# Revit family: FU_Chair_Sandler_Kicca 164
name_source: partatom
category: Furniture
units: mm (PartAtom-declared; Revit-internal decimal feet)

## family parameters
Always vertical = Yes
Cut with Voids When Loaded = No
OmniClass Number = 23.40.20.00
OmniClass Title = General Furniture and Specialties
Room Calculation Point = No
Shared = No
Work Plane-Based = No

## types (1)
- Kicca 164
    Default Elevation = 0 mm  [stored 0 ft]
    Depth = 570 mm  [stored 1.87008 ft]
    Description = Upholstered armchair on column steel base. 360° swivel without memory return.
    Frame Finish = Metal - Chrome - Polished
    Height = 760 mm
    Manufacturer = Sandler
    Model = Kicca 164
    Seat Material = Leather - Sandler 227
    URL = https://www.sandlerseating.com
    Width = 620 mm  [stored 2.03412 ft]

note: [stored X ft] marks values corroborated as IEEE doubles in the binary element streams (Revit-internal decimal feet)

## geometry (parser evidence)
native form markers: Sweep x6
no freeform markers — native parametric forms only
